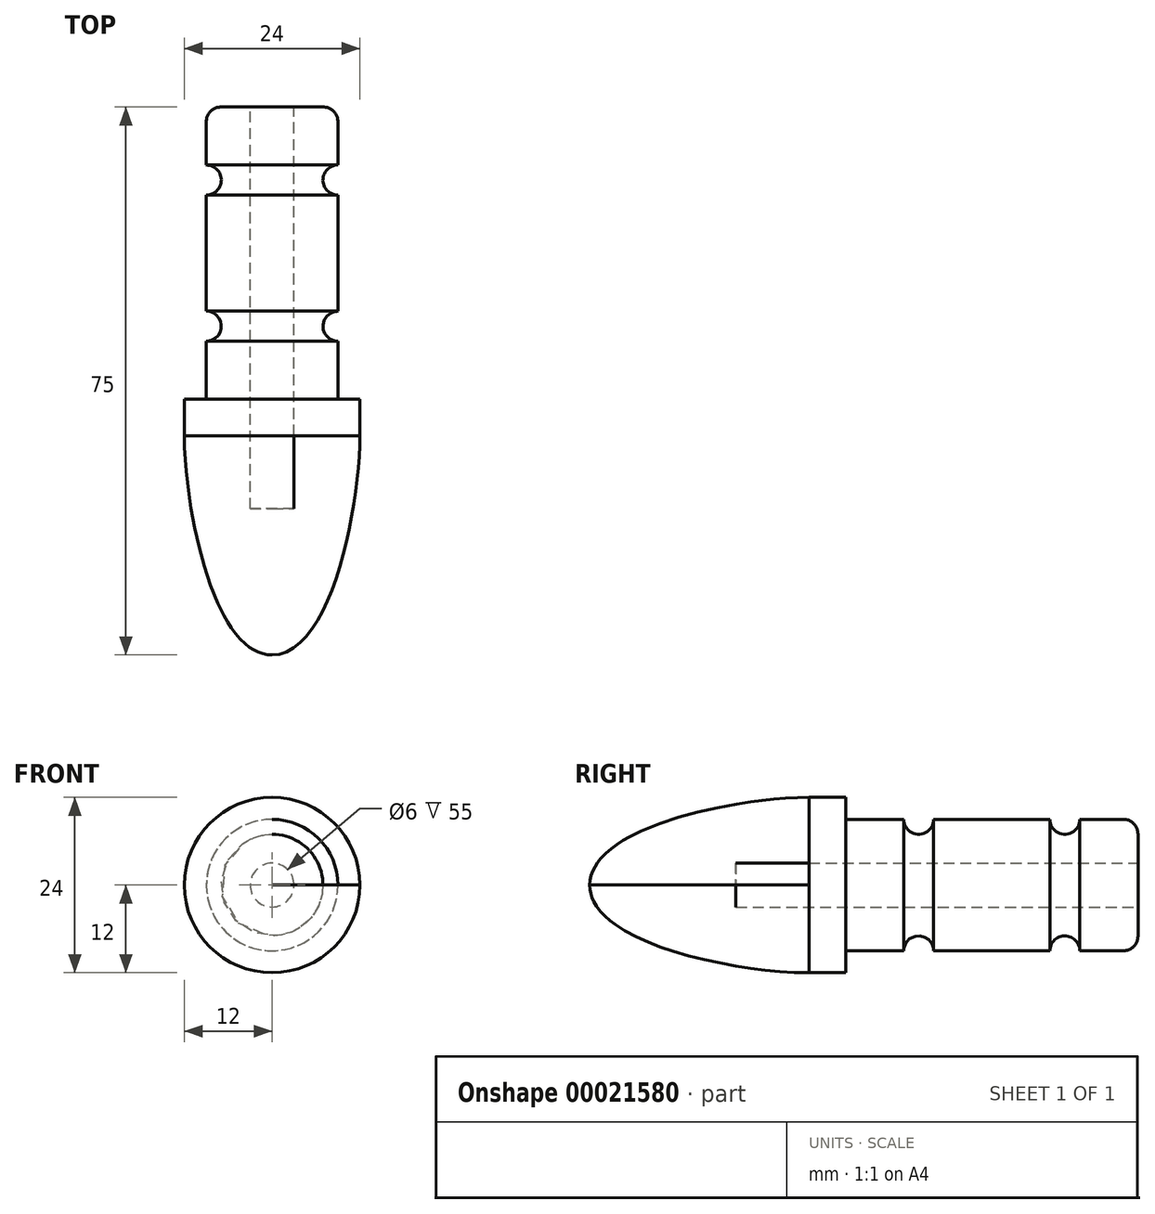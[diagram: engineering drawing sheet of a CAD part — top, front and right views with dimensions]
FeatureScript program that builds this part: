
annotation { "Feature Type Name" : "Feature", "Feature Type Description" : "" }
export const myFeature = defineFeature(function(context is Context, id is Id, definition is map)
    precondition{}
    {
        {
            var Q0;
            Q0=qCreatedBy(makeId("Top.planeOp"),FACE);
            var sketch = newSketch(context, id + "F0", { "sketchPlane" : qUnion([Q0])});
            skLineSegment(sketch, "E0", {"start": v(0, -55) * mm, "end": v(0, -75) * mm});
            skLineSegment(sketch, "E1", {"start": v(9, -2) * mm, "end": v(9, -40) * mm});
            skLineSegment(sketch, "E2", {"start": v(9, -40) * mm, "end": v(12, -40) * mm});
            skLineSegment(sketch, "E3", {"start": v(12, -40) * mm, "end": v(12, -45) * mm});
            skPoint(sketch, "E4", {"position": v(0, -75) * mm});
            skLineSegment(sketch, "E5", {"start": v(0, -75) * mm, "end": v(-13.94, -75) * mm, "construction": true});
            skFitSpline(sketch, "E6", {"points": [v(12, -45) * mm, v(0, -75) * mm], "startDerivative": vector(0, -30) * mm, "endDerivative": vector(-24, 0) * mm});
            skPoint(sketch, "E7.visualSharp", {"position": v(9, 0) * mm});
            skArc(sketch, "E7.filletArc", {"start": v(9, -2) * mm, "mid": v(8.41, -0.59) * mm, "end": v(7, 0) * mm});
            skLineSegment(sketch, "E8", {"start": v(3, -55) * mm, "end": v(0, -55) * mm});
            skPoint(sketch, "E9.orphan", {"position": v(0, 0) * mm});
            skLineSegment(sketch, "E10", {"start": v(0, -55) * mm, "end": v(0, 0) * mm, "construction": true});
            skLineSegment(sketch, "E11", {"start": v(3, 0) * mm, "end": v(3, -55) * mm});
            skLineSegment(sketch, "E12", {"start": v(3, 0) * mm, "end": v(7, 0) * mm});
            skSolve(sketch);
        }
        {
            var Q0;
            Q0=makeQuery(id+"F0.imprint","IMPRINT",FACE,{"disambiguationData":[TD([[makeQuery(id+"F0.imprint","IMPRINT",EDGE,{"derivedFrom":sQuery(id+"F0.wireOp",EDGE,"E0")}),1.0]])]});
            var Q1;
            Q1=sQuery(id+"F0.wireOp",EDGE,"E0");
            revolve(context, id + "F1", {"entities" : qUnion([Q0]), "axis" : qUnion([Q1]), "revolveType" : RevolveType.FULL});
        }
        {
            var Q0;
            Q0=qCreatedBy(makeId("Top.planeOp"),FACE);
            var sketch = newSketch(context, id + "F2", { "sketchPlane" : qUnion([Q0])});
            skArc(sketch, "E13", {"start": v(9, -7.95) * mm, "mid": v(6.95, -10) * mm, "end": v(9, -12.05) * mm});
            skLineSegment(sketch, "E14", {"start": v(9, -7.95) * mm, "end": v(19, -7.95) * mm});
            skLineSegment(sketch, "E15", {"start": v(19, -7.95) * mm, "end": v(19, -12.05) * mm});
            skLineSegment(sketch, "E16", {"start": v(19, -12.05) * mm, "end": v(9, -12.05) * mm});
            skArc(sketch, "E17", {"start": v(9, -27.95) * mm, "mid": v(6.95, -30) * mm, "end": v(9, -32.05) * mm});
            skLineSegment(sketch, "E18", {"start": v(9, -27.95) * mm, "end": v(19, -27.95) * mm});
            skLineSegment(sketch, "E19", {"start": v(19, -27.95) * mm, "end": v(19, -32.05) * mm});
            skLineSegment(sketch, "E20", {"start": v(19, -32.05) * mm, "end": v(9, -32.05) * mm});
            skSolve(sketch);
        }
        {
            var Q0;
            Q0=qSketchRegion(id+"F2",true);
            var Q1;
            Q1=sQuery(id+"F0.wireOp",EDGE,"E10");
            revolve(context, id + "F3", {"operationType" : NewBodyOperationType.REMOVE, "entities" : qUnion([Q0]), "axis" : qUnion([Q1]), "revolveType" : RevolveType.FULL, "oppositeDirection" : true});
        }
    });
